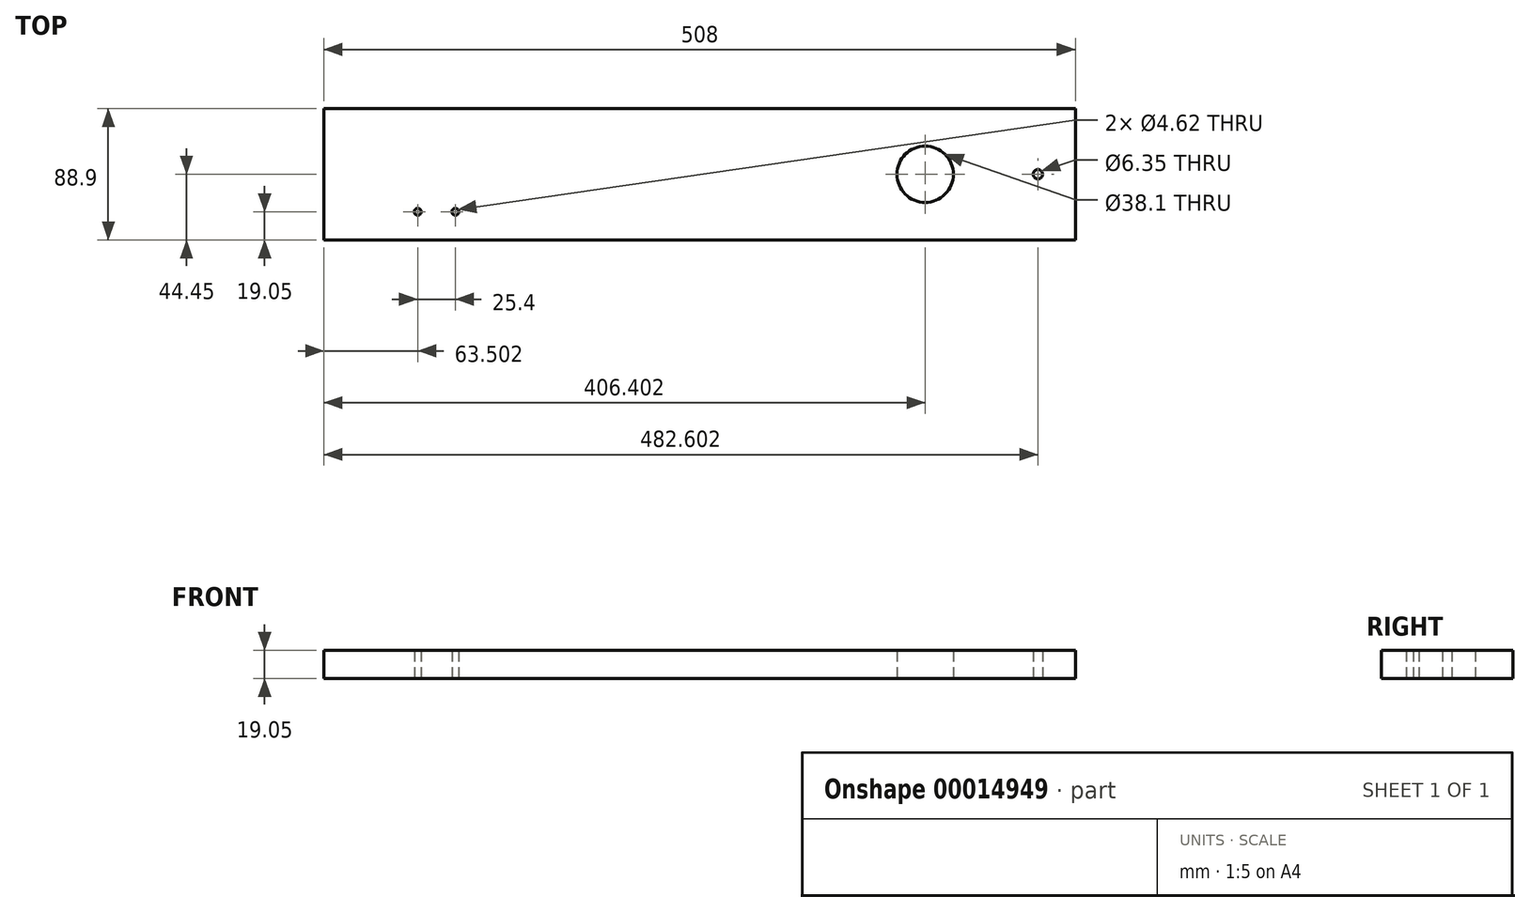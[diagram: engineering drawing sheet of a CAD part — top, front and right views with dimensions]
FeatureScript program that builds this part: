
annotation { "Feature Type Name" : "Feature", "Feature Type Description" : "" }
export const myFeature = defineFeature(function(context is Context, id is Id, definition is map)
    precondition{}
    {
        {
            var Q0;
            Q0=qCreatedBy(makeId("Top.planeOp"),FACE);
            var sketch = newSketch(context, id + "F0", { "sketchPlane" : qUnion([Q0])});
            skLineSegment(sketch, "E0.bottom", {"start": v(-118.25, 44.45) * mm, "end": v(389.75, 44.45) * mm});
            skLineSegment(sketch, "E0.top", {"start": v(-118.25, -44.45) * mm, "end": v(389.75, -44.45) * mm});
            skLineSegment(sketch, "E0.left", {"start": v(-118.25, 44.45) * mm, "end": v(-118.25, -44.45) * mm});
            skLineSegment(sketch, "E0.right", {"start": v(389.75, 44.45) * mm, "end": v(389.75, -44.45) * mm});
            skCircle(sketch, "E1", {"center": v(364.35, 0) * mm, "radius": 3.18 * mm});
            skCircle(sketch, "E2", {"center": v(288.15, 0) * mm, "radius": 19.05 * mm});
            skCircle(sketch, "E3", {"center": v(-54.75, -25.4) * mm, "radius": 2.31 * mm});
            skCircle(sketch, "E4", {"center": v(-29.35, -25.4) * mm, "radius": 2.31 * mm});
            skSolve(sketch);
        }
        {
            var Q0;
            Q0=makeQuery(id+"F0.imprint","IMPRINT",FACE,{"disambiguationData":[TD([[makeQuery(id+"F0.imprint","IMPRINT",EDGE,{"derivedFrom":sQuery(id+"F0.wireOp",EDGE,"E0.bottom")}),-1.0]])]});
            extrude(context, id + "F1", {"entities" : qUnion([Q0]), "depth" : 19.05 * mm});
        }
    });
